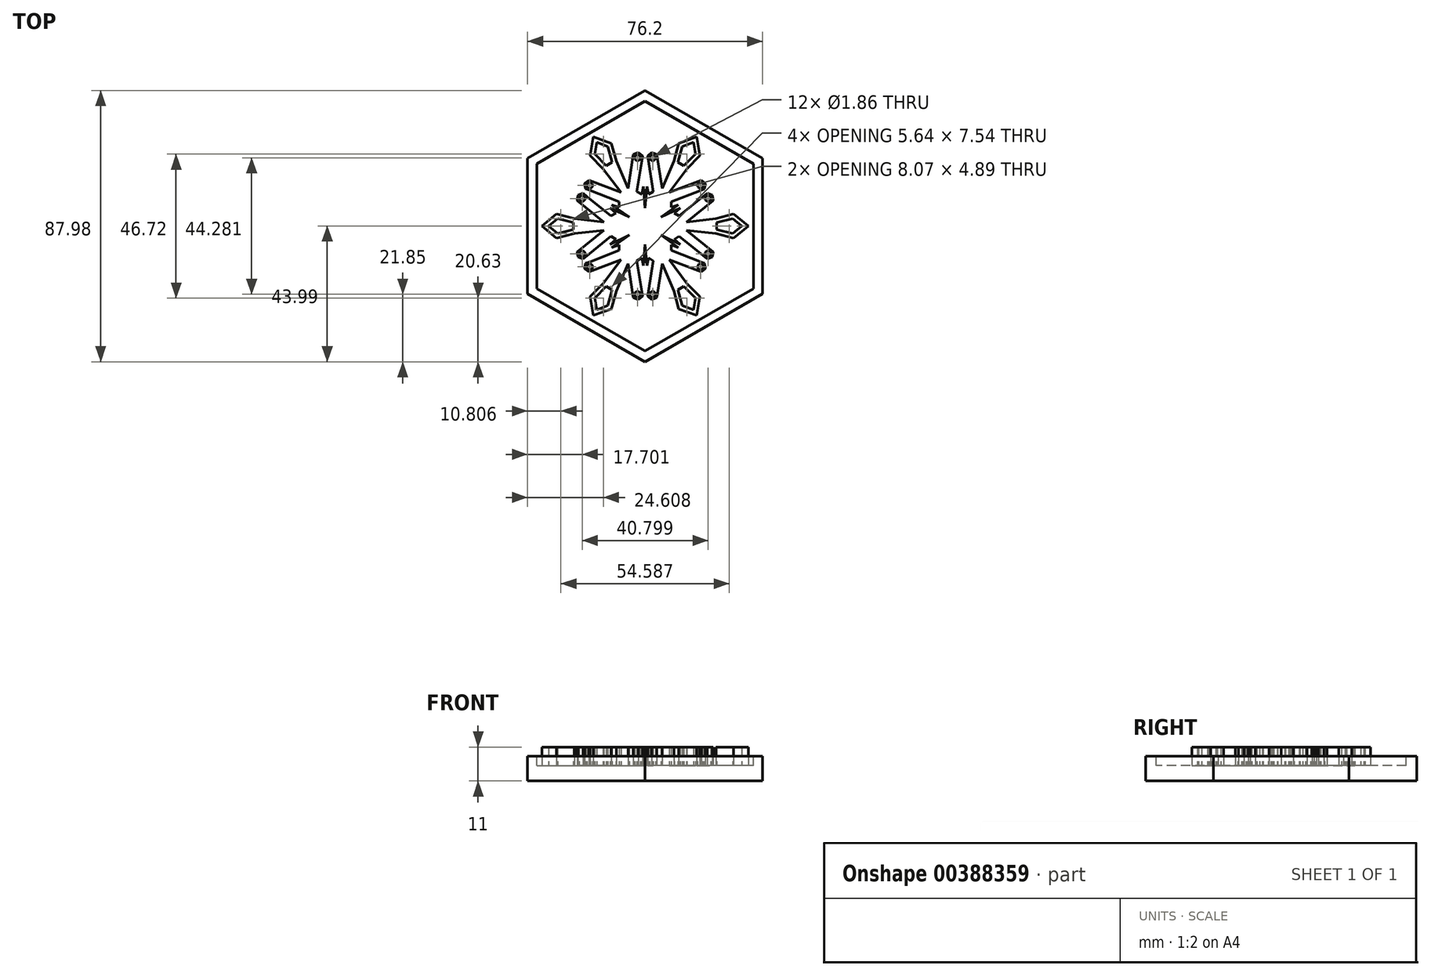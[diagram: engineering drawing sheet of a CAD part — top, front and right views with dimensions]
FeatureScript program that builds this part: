
annotation { "Feature Type Name" : "Feature", "Feature Type Description" : "" }
export const myFeature = defineFeature(function(context is Context, id is Id, definition is map)
    precondition{}
    {
        {
            var Q0;
            Q0=qCreatedBy(makeId("Top.planeOp"),FACE);
            var sketch = newSketch(context, id + "F0", { "sketchPlane" : qUnion([Q0])});
            skCircle(sketch, "E0.cCircle", {"center": v(0, 0) * mm, "radius": 38.1 * mm, "construction": true});
            skLineSegment(sketch, "E0.0", {"start": v(0, 44) * mm, "end": v(38.1, 22) * mm});
            skLineSegment(sketch, "E0.1", {"start": v(38.1, 22) * mm, "end": v(38.1, -22) * mm});
            skLineSegment(sketch, "E0.2", {"start": v(38.1, -22) * mm, "end": v(0, -44) * mm});
            skLineSegment(sketch, "E0.3", {"start": v(0, -44) * mm, "end": v(-38.1, -22) * mm});
            skLineSegment(sketch, "E0.4", {"start": v(-38.1, -22) * mm, "end": v(-38.1, 22) * mm});
            skLineSegment(sketch, "E0.5", {"start": v(-38.1, 22) * mm, "end": v(0, 44) * mm});
            skPoint(sketch, "E0.0.midPoint", {"position": v(19.05, 33) * mm});
            skLineSegment(sketch, "E1", {"start": v(0, 44) * mm, "end": v(0, -44) * mm, "construction": true});
            skLineSegment(sketch, "E2.0", {"start": v(35.1, 20.26) * mm, "end": v(35.1, -20.26) * mm});
            skLineSegment(sketch, "E2.1", {"start": v(0, -40.53) * mm, "end": v(-35.1, -20.26) * mm});
            skLineSegment(sketch, "E2.2", {"start": v(-35.1, -20.26) * mm, "end": v(-35.1, 20.26) * mm});
            skLineSegment(sketch, "E2.3", {"start": v(35.1, -20.26) * mm, "end": v(0, -40.53) * mm});
            skLineSegment(sketch, "E2.4", {"start": v(-35.1, 20.26) * mm, "end": v(0, 40.53) * mm});
            skLineSegment(sketch, "E2.5", {"start": v(0, 40.53) * mm, "end": v(35.1, 20.26) * mm});
            skSolve(sketch);
        }
        {
            var Q0;
            Q0 = qSketchRegion(id + "F0", true);
            var Q1;
            Q1=makeQuery(id+"F0.imprint","IMPRINT",FACE,{"disambiguationData":[TD([[makeQuery(id+"F0.imprint","IMPRINT",EDGE,{"derivedFrom":sQuery(id+"F0.wireOp",EDGE,"E2.0")}),-1.0]])]});
            extrude(context, id + "F1", {"entities" : qUnion([Q0, Q1]), "oppositeDirection" : true, "depth" : 8 * mm});
        }
        {
            var Q0;
            Q0=makeQuery(id+"F0.imprint","IMPRINT",FACE,{"disambiguationData":[TD([[makeQuery(id+"F0.imprint","IMPRINT",EDGE,{"derivedFrom":sQuery(id+"F0.wireOp",EDGE,"E2.0")}),-1.0]])]});
            extrude(context, id + "F2", {"entities" : qUnion([Q0]), "operationType" : NewBodyOperationType.REMOVE, "oppositeDirection" : true, "depth" : 3 * mm});
        }
        {
            var Q0;
            Q0=makeQuery(id+"F2.boolean.opBoolean","COPY",FACE,{"derivedFrom":makeQuery(id+"F2.opExtrude","CAP_FACE",FACE,{"disambiguationData":[OSD([sQuery(id+"F0.wireOp",EDGE,"E2.0"),sQuery(id+"F0.wireOp",EDGE,"E2.1"),sQuery(id+"F0.wireOp",EDGE,"E2.2"),sQuery(id+"F0.wireOp",EDGE,"E2.3"),sQuery(id+"F0.wireOp",EDGE,"E2.4"),sQuery(id+"F0.wireOp",EDGE,"E2.5")])],"isStart":false})});
            var sketch = newSketch(context, id + "F3", { "sketchPlane" : qUnion([Q0])});
            skLineSegment(sketch, "E3.0", {"start": v(0, 5.78) * mm, "end": v(5, 2.9) * mm});
            skLineSegment(sketch, "E3.1", {"start": v(5, 2.9) * mm, "end": v(5, -2.88) * mm});
            skLineSegment(sketch, "E3.2", {"start": v(5, -2.88) * mm, "end": v(0, -5.76) * mm});
            skLineSegment(sketch, "E3.3", {"start": v(0, -5.76) * mm, "end": v(-5, -2.88) * mm});
            skLineSegment(sketch, "E3.4", {"start": v(-5, -2.88) * mm, "end": v(-5, 2.9) * mm});
            skLineSegment(sketch, "E3.5", {"start": v(-5, 2.9) * mm, "end": v(0, 5.78) * mm});
            skPoint(sketch, "E3.0.midPoint", {"position": v(2.5, 4.34) * mm});
            skLineSegment(sketch, "E4", {"start": v(-16.74, -29) * mm, "end": v(0, 0) * mm, "construction": true});
            skLineSegment(sketch, "E5", {"start": v(-16.74, -29) * mm, "end": v(-17.8, -22.9) * mm});
            skLineSegment(sketch, "E6", {"start": v(-17.8, -22.9) * mm, "end": v(-13.57, -18.62) * mm});
            skLineSegment(sketch, "E7", {"start": v(-13.57, -18.62) * mm, "end": v(-7.83, -10.9) * mm});
            skLineSegment(sketch, "E8", {"start": v(-8.4, -7.92) * mm, "end": v(-8.4, -6.07) * mm});
            skLineSegment(sketch, "E9", {"start": v(-8.4, -6.07) * mm, "end": v(-10.81, -6.92) * mm});
            skLineSegment(sketch, "E10", {"start": v(-10.81, -6.92) * mm, "end": v(-5, -2.88) * mm});
            skLineSegment(sketch, "E11.MirrorCS", {"start": v(-16.74, -29) * mm, "end": v(-10.93, -26.86) * mm});
            skLineSegment(sketch, "E12.MirrorCS", {"start": v(-10.93, -26.86) * mm, "end": v(-9.34, -21.06) * mm});
            skLineSegment(sketch, "E13.MirrorCS", {"start": v(-9.34, -21.06) * mm, "end": v(-5.52, -12.23) * mm});
            skLineSegment(sketch, "E14.MirrorCS", {"start": v(-2.65, -11.24) * mm, "end": v(-1.06, -10.32) * mm});
            skLineSegment(sketch, "E15.MirrorCS", {"start": v(-1.06, -10.32) * mm, "end": v(-0.59, -12.83) * mm});
            skLineSegment(sketch, "E16.MirrorCS", {"start": v(-0.59, -12.83) * mm, "end": v(0.01, -5.77) * mm});
            skPoint(sketch, "E17.center", {"position": v(0, 0) * mm});
            skLineSegment(sketch, "E18", {"start": v(-7.83, -10.9) * mm, "end": v(-17.41, -14.6) * mm});
            skLineSegment(sketch, "E19", {"start": v(-18.49, -11.8) * mm, "end": v(-8.4, -7.92) * mm});
            skArc(sketch, "E20.cCircle", {"start": v(-18.49, -11.8) * mm, "mid": v(-18.49, -11.8) * mm, "end": v(-18.49, -11.8) * mm, "construction": true});
            skLineSegment(sketch, "E20.0", {"start": v(-19.3, -12.1) * mm, "end": v(-17.68, -11.48) * mm});
            skLineSegment(sketch, "E20.1", {"start": v(-17.68, -11.48) * mm, "end": v(-17.68, -11.48) * mm});
            skLineSegment(sketch, "E20.3", {"start": v(-16.6, -14.28) * mm, "end": v(-18.22, -14.9) * mm});
            skLineSegment(sketch, "E20.4", {"start": v(-18.22, -14.9) * mm, "end": v(-19.57, -13.81) * mm});
            skLineSegment(sketch, "E20.5", {"start": v(-19.57, -13.81) * mm, "end": v(-19.3, -12.1) * mm});
            skPoint(sketch, "E20.0.midPoint", {"position": v(-18.49, -11.8) * mm});
            skPoint(sketch, "E21.orphan", {"position": v(-16.33, -12.57) * mm});
            skLineSegment(sketch, "E22.MirrorCS", {"start": v(-5.52, -12.23) * mm, "end": v(-3.93, -22.37) * mm});
            skLineSegment(sketch, "E23.MirrorCS", {"start": v(-3.8, -23.23) * mm, "end": v(-2.18, -23.85) * mm});
            skLineSegment(sketch, "E24.MirrorCS", {"start": v(-2.18, -23.85) * mm, "end": v(-0.83, -22.76) * mm});
            skLineSegment(sketch, "E25.MirrorCS", {"start": v(-0.97, -21.9) * mm, "end": v(-2.65, -11.24) * mm});
            skLineSegment(sketch, "E26.MirrorCS", {"start": v(-4.06, -21.52) * mm, "end": v(-3.8, -23.23) * mm});
            skLineSegment(sketch, "E27.MirrorCS", {"start": v(-0.83, -22.76) * mm, "end": v(-1.1, -21.05) * mm});
            skLineSegment(sketch, "E28.0", {"start": v(-16.31, -23.36) * mm, "end": v(-12.59, -19.59) * mm});
            skLineSegment(sketch, "E28.1", {"start": v(-15.66, -27.13) * mm, "end": v(-16.31, -23.36) * mm});
            skLineSegment(sketch, "E28.2", {"start": v(-15.66, -27.13) * mm, "end": v(-12.08, -25.8) * mm});
            skLineSegment(sketch, "E28.3", {"start": v(-12.08, -25.8) * mm, "end": v(-10.67, -20.7) * mm});
            skLineSegment(sketch, "E29", {"start": v(-12.59, -19.59) * mm, "end": v(-10.67, -20.7) * mm});
            skLineSegment(sketch, "E30", {"start": v(-2.18, -23.85) * mm, "end": v(-2.8, -19.92) * mm, "construction": true});
            skLineSegment(sketch, "E31", {"start": v(-2.8, -19.92) * mm, "end": v(-0.97, -21.9) * mm, "construction": true});
            skLineSegment(sketch, "E32", {"start": v(-0.97, -21.9) * mm, "end": v(-3.93, -22.37) * mm, "construction": true});
            skCircle(sketch, "E33", {"center": v(-2.45, -22.14) * mm, "radius": 0.93 * mm});
            skCircle(sketch, "E34.MirrorC", {"center": v(-17.95, -13.2) * mm, "radius": 0.93 * mm});
            skLineSegment(sketch, "E35.0", {"start": v(-7.4, -7.92) * mm, "end": v(-7.4, -5.77) * mm});
            skLineSegment(sketch, "E36.0", {"start": v(-3.15, -10.37) * mm, "end": v(-1.3, -9.3) * mm});
            skLineSegment(sketch, "E37.0", {"start": v(-1.3, -9.3) * mm, "end": v(-1.04, -6.32) * mm});
            skLineSegment(sketch, "E38.0", {"start": v(-1.04, -6.32) * mm, "end": v(-4.95, -4.06) * mm});
            skLineSegment(sketch, "E39.trimOffspring", {"start": v(-7.4, -5.77) * mm, "end": v(-4.95, -4.06) * mm});
            skLineSegment(sketch, "E40", {"start": v(-7.4, -7.92) * mm, "end": v(-6.38, -11.05) * mm});
            skLineSegment(sketch, "E41.MirrorCS", {"start": v(-3.15, -10.37) * mm, "end": v(-6.38, -11.05) * mm});
            skLineSegment(sketch, "E42.1.1", {"start": v(16.74, -29) * mm, "end": v(17.8, -22.9) * mm});
            skLineSegment(sketch, "E42.1.2", {"start": v(0.97, -21.9) * mm, "end": v(2.65, -11.24) * mm});
            skLineSegment(sketch, "E42.1.3", {"start": v(13.57, -18.62) * mm, "end": v(7.83, -10.9) * mm});
            skPoint(sketch, "E42.1.4", {"position": v(2.72, -20.43) * mm});
            skPoint(sketch, "E42.1.5", {"position": v(0.97, -21.9) * mm});
            skLineSegment(sketch, "E42.1.6", {"start": v(7.4, -7.92) * mm, "end": v(6.38, -11.05) * mm});
            skLineSegment(sketch, "E42.1.7", {"start": v(17.8, -22.9) * mm, "end": v(13.57, -18.62) * mm});
            skLineSegment(sketch, "E42.1.8", {"start": v(1.3, -9.3) * mm, "end": v(1.04, -6.32) * mm});
            skLineSegment(sketch, "E42.1.9", {"start": v(7.83, -10.9) * mm, "end": v(17.41, -14.6) * mm});
            skLineSegment(sketch, "E42.1.10", {"start": v(18.49, -11.8) * mm, "end": v(8.4, -7.92) * mm});
            skLineSegment(sketch, "E42.1.11", {"start": v(12.08, -25.8) * mm, "end": v(10.67, -20.7) * mm});
            skLineSegment(sketch, "E42.1.12", {"start": v(3.15, -10.37) * mm, "end": v(6.38, -11.05) * mm});
            skLineSegment(sketch, "E42.1.13", {"start": v(0.59, -12.83) * mm, "end": v(-0.01, -5.77) * mm});
            skLineSegment(sketch, "E42.1.14", {"start": v(9.34, -21.06) * mm, "end": v(5.52, -12.23) * mm});
            skLineSegment(sketch, "E42.1.15", {"start": v(15.66, -27.13) * mm, "end": v(16.31, -23.36) * mm});
            skLineSegment(sketch, "E42.1.16", {"start": v(10.93, -26.86) * mm, "end": v(9.34, -21.06) * mm});
            skLineSegment(sketch, "E42.1.17", {"start": v(16.74, -29) * mm, "end": v(10.93, -26.86) * mm});
            skLineSegment(sketch, "E42.1.18", {"start": v(5.52, -12.23) * mm, "end": v(3.93, -22.37) * mm});
            skLineSegment(sketch, "E42.1.19", {"start": v(16.31, -23.36) * mm, "end": v(12.59, -19.59) * mm});
            skLineSegment(sketch, "E42.1.20", {"start": v(15.66, -27.13) * mm, "end": v(12.08, -25.8) * mm});
            skLineSegment(sketch, "E42.1.21", {"start": v(4.06, -21.52) * mm, "end": v(3.8, -23.23) * mm});
            skCircle(sketch, "E42.1.22", {"center": v(2.45, -22.14) * mm, "radius": 0.93 * mm});
            skLineSegment(sketch, "E42.1.23", {"start": v(19.57, -13.81) * mm, "end": v(15.85, -12.39) * mm, "construction": true});
            skLineSegment(sketch, "E42.1.24", {"start": v(16.6, -14.28) * mm, "end": v(18.22, -14.9) * mm});
            skLineSegment(sketch, "E42.1.25", {"start": v(3.8, -23.23) * mm, "end": v(2.18, -23.85) * mm});
            skCircle(sketch, "E42.1.26", {"center": v(17.95, -13.2) * mm, "radius": 0.93 * mm});
            skLineSegment(sketch, "E42.1.27", {"start": v(15.85, -12.39) * mm, "end": v(18.49, -11.8) * mm, "construction": true});
            skLineSegment(sketch, "E42.1.28", {"start": v(2.18, -23.85) * mm, "end": v(0.83, -22.76) * mm});
            skLineSegment(sketch, "E42.1.29", {"start": v(2.65, -11.24) * mm, "end": v(1.06, -10.32) * mm});
            skLineSegment(sketch, "E42.1.30", {"start": v(19.57, -13.81) * mm, "end": v(19.3, -12.1) * mm});
            skLineSegment(sketch, "E42.1.31", {"start": v(7.4, -7.92) * mm, "end": v(7.4, -5.77) * mm});
            skLineSegment(sketch, "E42.1.32", {"start": v(10.67, -20.7) * mm, "end": v(12.59, -19.59) * mm});
            skLineSegment(sketch, "E42.1.33", {"start": v(8.4, -6.07) * mm, "end": v(10.81, -6.92) * mm});
            skLineSegment(sketch, "E42.1.34", {"start": v(18.49, -11.8) * mm, "end": v(17.41, -14.6) * mm, "construction": true});
            skLineSegment(sketch, "E42.1.35", {"start": v(3.15, -10.37) * mm, "end": v(1.3, -9.3) * mm});
            skLineSegment(sketch, "E42.1.36", {"start": v(8.4, -7.92) * mm, "end": v(8.4, -6.07) * mm});
            skLineSegment(sketch, "E42.1.37", {"start": v(1.06, -10.32) * mm, "end": v(0.59, -12.83) * mm});
            skLineSegment(sketch, "E42.1.38", {"start": v(19.3, -12.1) * mm, "end": v(17.68, -11.48) * mm});
            skLineSegment(sketch, "E42.1.39", {"start": v(18.22, -14.9) * mm, "end": v(19.57, -13.81) * mm});
            skLineSegment(sketch, "E42.1.40", {"start": v(0.83, -22.76) * mm, "end": v(1.1, -21.05) * mm});
            skLineSegment(sketch, "E42.1.41", {"start": v(1.1, -21.05) * mm, "end": v(1.1, -21.05) * mm});
            skArc(sketch, "E42.1.42", {"start": v(0.97, -21.9) * mm, "mid": v(0.97, -21.9) * mm, "end": v(0.97, -21.9) * mm, "construction": true});
            skLineSegment(sketch, "E42.1.43", {"start": v(10.81, -6.92) * mm, "end": v(5, -2.88) * mm});
            skLineSegment(sketch, "E42.1.44", {"start": v(7.4, -5.77) * mm, "end": v(4.95, -4.06) * mm});
            skLineSegment(sketch, "E42.1.45", {"start": v(4.95, -4.06) * mm, "end": v(1.04, -6.32) * mm});
            skLineSegment(sketch, "E42.2.1", {"start": v(33.49, 0) * mm, "end": v(28.73, 3.96) * mm});
            skLineSegment(sketch, "E42.2.2", {"start": v(19.46, -10.12) * mm, "end": v(11.06, -3.32) * mm});
            skLineSegment(sketch, "E42.2.3", {"start": v(22.9, 2.44) * mm, "end": v(13.36, 1.33) * mm});
            skPoint(sketch, "E42.2.4", {"position": v(19.05, -7.86) * mm});
            skPoint(sketch, "E42.2.5", {"position": v(19.46, -10.12) * mm});
            skLineSegment(sketch, "E42.2.6", {"start": v(10.56, 2.45) * mm, "end": v(12.76, 0) * mm});
            skLineSegment(sketch, "E42.2.7", {"start": v(28.73, 3.96) * mm, "end": v(22.9, 2.44) * mm});
            skLineSegment(sketch, "E42.2.8", {"start": v(8.7, -3.53) * mm, "end": v(6, -2.26) * mm});
            skLineSegment(sketch, "E42.2.9", {"start": v(13.36, 1.33) * mm, "end": v(21.34, 7.78) * mm});
            skLineSegment(sketch, "E42.2.10", {"start": v(19.46, 10.12) * mm, "end": v(11.06, 3.32) * mm});
            skLineSegment(sketch, "E42.2.11", {"start": v(28.4, -2.45) * mm, "end": v(23.26, -1.1) * mm});
            skLineSegment(sketch, "E42.2.12", {"start": v(10.56, -2.45) * mm, "end": v(12.76, 0) * mm});
            skLineSegment(sketch, "E42.2.13", {"start": v(11.4, -5.9) * mm, "end": v(5, -2.9) * mm});
            skLineSegment(sketch, "E42.2.14", {"start": v(22.9, -2.44) * mm, "end": v(13.36, -1.33) * mm});
            skLineSegment(sketch, "E42.2.15", {"start": v(31.33, 0) * mm, "end": v(28.4, 2.45) * mm});
            skLineSegment(sketch, "E42.2.16", {"start": v(28.73, -3.96) * mm, "end": v(22.9, -2.44) * mm});
            skLineSegment(sketch, "E42.2.17", {"start": v(33.49, 0) * mm, "end": v(28.73, -3.96) * mm});
            skLineSegment(sketch, "E42.2.18", {"start": v(13.36, -1.33) * mm, "end": v(21.34, -7.78) * mm});
            skLineSegment(sketch, "E42.2.19", {"start": v(28.4, 2.45) * mm, "end": v(23.26, 1.1) * mm});
            skLineSegment(sketch, "E42.2.20", {"start": v(31.33, 0) * mm, "end": v(28.4, -2.45) * mm});
            skLineSegment(sketch, "E42.2.21", {"start": v(20.67, -7.24) * mm, "end": v(22.01, -8.33) * mm});
            skCircle(sketch, "E42.2.22", {"center": v(20.4, -8.95) * mm, "radius": 0.93 * mm});
            skLineSegment(sketch, "E42.2.23", {"start": v(21.75, 10.04) * mm, "end": v(18.65, 7.53) * mm, "construction": true});
            skLineSegment(sketch, "E42.2.24", {"start": v(20.67, 7.24) * mm, "end": v(22.01, 8.33) * mm});
            skLineSegment(sketch, "E42.2.25", {"start": v(22.01, -8.33) * mm, "end": v(21.75, -10.04) * mm});
            skCircle(sketch, "E42.2.26", {"center": v(20.4, 8.95) * mm, "radius": 0.93 * mm});
            skLineSegment(sketch, "E42.2.27", {"start": v(18.65, 7.53) * mm, "end": v(19.46, 10.12) * mm, "construction": true});
            skLineSegment(sketch, "E42.2.28", {"start": v(21.75, -10.04) * mm, "end": v(20.13, -10.66) * mm});
            skLineSegment(sketch, "E42.2.29", {"start": v(11.06, -3.32) * mm, "end": v(9.46, -4.24) * mm});
            skLineSegment(sketch, "E42.2.30", {"start": v(21.75, 10.04) * mm, "end": v(20.13, 10.66) * mm});
            skLineSegment(sketch, "E42.2.31", {"start": v(10.56, 2.45) * mm, "end": v(8.7, 3.53) * mm});
            skLineSegment(sketch, "E42.2.32", {"start": v(23.26, -1.1) * mm, "end": v(23.26, 1.1) * mm});
            skLineSegment(sketch, "E42.2.33", {"start": v(9.46, 4.24) * mm, "end": v(11.4, 5.9) * mm});
            skLineSegment(sketch, "E42.2.34", {"start": v(19.46, 10.12) * mm, "end": v(21.34, 7.78) * mm, "construction": true});
            skLineSegment(sketch, "E42.2.35", {"start": v(10.56, -2.45) * mm, "end": v(8.7, -3.53) * mm});
            skLineSegment(sketch, "E42.2.36", {"start": v(11.06, 3.32) * mm, "end": v(9.46, 4.24) * mm});
            skLineSegment(sketch, "E42.2.37", {"start": v(9.46, -4.24) * mm, "end": v(11.4, -5.9) * mm});
            skLineSegment(sketch, "E42.2.38", {"start": v(20.13, 10.66) * mm, "end": v(18.78, 9.57) * mm});
            skLineSegment(sketch, "E42.2.39", {"start": v(22.01, 8.33) * mm, "end": v(21.75, 10.04) * mm});
            skLineSegment(sketch, "E42.2.40", {"start": v(20.13, -10.66) * mm, "end": v(18.78, -9.57) * mm});
            skLineSegment(sketch, "E42.2.41", {"start": v(18.78, -9.57) * mm, "end": v(18.78, -9.57) * mm});
            skArc(sketch, "E42.2.42", {"start": v(19.45, -10.11) * mm, "mid": v(19.45, -10.11) * mm, "end": v(19.46, -10.12) * mm, "construction": true});
            skLineSegment(sketch, "E42.2.43", {"start": v(11.4, 5.9) * mm, "end": v(5, 2.9) * mm});
            skLineSegment(sketch, "E42.2.44", {"start": v(8.7, 3.53) * mm, "end": v(6, 2.26) * mm});
            skLineSegment(sketch, "E42.2.45", {"start": v(6, 2.26) * mm, "end": v(6, -2.26) * mm});
            skLineSegment(sketch, "E42.3.1", {"start": v(16.74, 29) * mm, "end": v(10.93, 26.86) * mm});
            skLineSegment(sketch, "E42.3.2", {"start": v(18.49, 11.8) * mm, "end": v(8.4, 7.92) * mm});
            skLineSegment(sketch, "E42.3.3", {"start": v(9.34, 21.06) * mm, "end": v(5.52, 12.23) * mm});
            skPoint(sketch, "E42.3.4", {"position": v(16.33, 12.57) * mm});
            skPoint(sketch, "E42.3.5", {"position": v(18.49, 11.8) * mm});
            skLineSegment(sketch, "E42.3.6", {"start": v(3.15, 10.37) * mm, "end": v(6.38, 11.05) * mm});
            skLineSegment(sketch, "E42.3.7", {"start": v(10.93, 26.86) * mm, "end": v(9.34, 21.06) * mm});
            skLineSegment(sketch, "E42.3.8", {"start": v(7.4, 5.77) * mm, "end": v(4.95, 4.06) * mm});
            skLineSegment(sketch, "E42.3.9", {"start": v(5.52, 12.23) * mm, "end": v(3.93, 22.37) * mm});
            skLineSegment(sketch, "E42.3.10", {"start": v(0.97, 21.9) * mm, "end": v(2.65, 11.24) * mm});
            skLineSegment(sketch, "E42.3.11", {"start": v(16.31, 23.36) * mm, "end": v(12.59, 19.59) * mm});
            skLineSegment(sketch, "E42.3.12", {"start": v(7.4, 7.92) * mm, "end": v(6.38, 11.05) * mm});
            skLineSegment(sketch, "E42.3.13", {"start": v(10.81, 6.92) * mm, "end": v(5, 2.88) * mm});
            skLineSegment(sketch, "E42.3.14", {"start": v(13.57, 18.62) * mm, "end": v(7.83, 10.9) * mm});
            skLineSegment(sketch, "E42.3.15", {"start": v(15.66, 27.13) * mm, "end": v(12.08, 25.8) * mm});
            skLineSegment(sketch, "E42.3.16", {"start": v(17.8, 22.9) * mm, "end": v(13.57, 18.62) * mm});
            skLineSegment(sketch, "E42.3.17", {"start": v(16.74, 29) * mm, "end": v(17.8, 22.9) * mm});
            skLineSegment(sketch, "E42.3.18", {"start": v(7.83, 10.9) * mm, "end": v(17.41, 14.6) * mm});
            skLineSegment(sketch, "E42.3.19", {"start": v(12.08, 25.8) * mm, "end": v(10.67, 20.7) * mm});
            skLineSegment(sketch, "E42.3.20", {"start": v(15.66, 27.13) * mm, "end": v(16.31, 23.36) * mm});
            skLineSegment(sketch, "E42.3.21", {"start": v(16.6, 14.28) * mm, "end": v(18.22, 14.9) * mm});
            skCircle(sketch, "E42.3.22", {"center": v(17.95, 13.2) * mm, "radius": 0.93 * mm});
            skLineSegment(sketch, "E42.3.23", {"start": v(2.18, 23.85) * mm, "end": v(2.8, 19.92) * mm, "construction": true});
            skLineSegment(sketch, "E42.3.24", {"start": v(4.06, 21.52) * mm, "end": v(3.8, 23.23) * mm});
            skLineSegment(sketch, "E42.3.25", {"start": v(18.22, 14.9) * mm, "end": v(19.57, 13.81) * mm});
            skCircle(sketch, "E42.3.26", {"center": v(2.45, 22.14) * mm, "radius": 0.93 * mm});
            skLineSegment(sketch, "E42.3.27", {"start": v(2.8, 19.92) * mm, "end": v(0.97, 21.9) * mm, "construction": true});
            skLineSegment(sketch, "E42.3.28", {"start": v(19.57, 13.81) * mm, "end": v(19.3, 12.1) * mm});
            skLineSegment(sketch, "E42.3.29", {"start": v(8.4, 7.92) * mm, "end": v(8.4, 6.07) * mm});
            skLineSegment(sketch, "E42.3.30", {"start": v(2.18, 23.85) * mm, "end": v(0.83, 22.76) * mm});
            skLineSegment(sketch, "E42.3.31", {"start": v(3.15, 10.37) * mm, "end": v(1.3, 9.3) * mm});
            skLineSegment(sketch, "E42.3.32", {"start": v(12.59, 19.59) * mm, "end": v(10.67, 20.7) * mm});
            skLineSegment(sketch, "E42.3.33", {"start": v(1.06, 10.32) * mm, "end": v(0.59, 12.83) * mm});
            skLineSegment(sketch, "E42.3.34", {"start": v(0.97, 21.9) * mm, "end": v(3.93, 22.37) * mm, "construction": true});
            skLineSegment(sketch, "E42.3.35", {"start": v(7.4, 7.92) * mm, "end": v(7.4, 5.77) * mm});
            skLineSegment(sketch, "E42.3.36", {"start": v(2.65, 11.24) * mm, "end": v(1.06, 10.32) * mm});
            skLineSegment(sketch, "E42.3.37", {"start": v(8.4, 6.07) * mm, "end": v(10.81, 6.92) * mm});
            skLineSegment(sketch, "E42.3.38", {"start": v(0.83, 22.76) * mm, "end": v(1.1, 21.05) * mm});
            skLineSegment(sketch, "E42.3.39", {"start": v(3.8, 23.23) * mm, "end": v(2.18, 23.85) * mm});
            skLineSegment(sketch, "E42.3.40", {"start": v(19.3, 12.1) * mm, "end": v(17.68, 11.48) * mm});
            skLineSegment(sketch, "E42.3.41", {"start": v(17.68, 11.48) * mm, "end": v(17.68, 11.48) * mm});
            skArc(sketch, "E42.3.42", {"start": v(18.49, 11.8) * mm, "mid": v(18.49, 11.8) * mm, "end": v(18.49, 11.8) * mm, "construction": true});
            skLineSegment(sketch, "E42.3.43", {"start": v(0.59, 12.83) * mm, "end": v(-0.01, 5.77) * mm});
            skLineSegment(sketch, "E42.3.44", {"start": v(1.3, 9.3) * mm, "end": v(1.04, 6.32) * mm});
            skLineSegment(sketch, "E42.3.45", {"start": v(1.04, 6.32) * mm, "end": v(4.95, 4.06) * mm});
            skLineSegment(sketch, "E42.4.1", {"start": v(-16.74, 29) * mm, "end": v(-17.8, 22.9) * mm});
            skLineSegment(sketch, "E42.4.2", {"start": v(-0.97, 21.9) * mm, "end": v(-2.65, 11.24) * mm});
            skLineSegment(sketch, "E42.4.3", {"start": v(-13.57, 18.62) * mm, "end": v(-7.83, 10.9) * mm});
            skPoint(sketch, "E42.4.4", {"position": v(-2.72, 20.43) * mm});
            skPoint(sketch, "E42.4.5", {"position": v(-0.97, 21.9) * mm});
            skLineSegment(sketch, "E42.4.6", {"start": v(-7.4, 7.92) * mm, "end": v(-6.38, 11.05) * mm});
            skLineSegment(sketch, "E42.4.7", {"start": v(-17.8, 22.9) * mm, "end": v(-13.57, 18.62) * mm});
            skLineSegment(sketch, "E42.4.8", {"start": v(-1.3, 9.3) * mm, "end": v(-1.04, 6.32) * mm});
            skLineSegment(sketch, "E42.4.9", {"start": v(-7.83, 10.9) * mm, "end": v(-17.41, 14.6) * mm});
            skLineSegment(sketch, "E42.4.10", {"start": v(-18.49, 11.8) * mm, "end": v(-8.4, 7.92) * mm});
            skLineSegment(sketch, "E42.4.11", {"start": v(-12.08, 25.8) * mm, "end": v(-10.67, 20.7) * mm});
            skLineSegment(sketch, "E42.4.12", {"start": v(-3.15, 10.37) * mm, "end": v(-6.38, 11.05) * mm});
            skLineSegment(sketch, "E42.4.13", {"start": v(-0.59, 12.83) * mm, "end": v(0.01, 5.77) * mm});
            skLineSegment(sketch, "E42.4.14", {"start": v(-9.34, 21.06) * mm, "end": v(-5.52, 12.23) * mm});
            skLineSegment(sketch, "E42.4.15", {"start": v(-15.66, 27.13) * mm, "end": v(-16.31, 23.36) * mm});
            skLineSegment(sketch, "E42.4.16", {"start": v(-10.93, 26.86) * mm, "end": v(-9.34, 21.06) * mm});
            skLineSegment(sketch, "E42.4.17", {"start": v(-16.74, 29) * mm, "end": v(-10.93, 26.86) * mm});
            skLineSegment(sketch, "E42.4.18", {"start": v(-5.52, 12.23) * mm, "end": v(-3.93, 22.37) * mm});
            skLineSegment(sketch, "E42.4.19", {"start": v(-16.31, 23.36) * mm, "end": v(-12.59, 19.59) * mm});
            skLineSegment(sketch, "E42.4.20", {"start": v(-15.66, 27.13) * mm, "end": v(-12.08, 25.8) * mm});
            skLineSegment(sketch, "E42.4.21", {"start": v(-4.06, 21.52) * mm, "end": v(-3.8, 23.23) * mm});
            skCircle(sketch, "E42.4.22", {"center": v(-2.45, 22.14) * mm, "radius": 0.93 * mm});
            skLineSegment(sketch, "E42.4.23", {"start": v(-19.57, 13.81) * mm, "end": v(-15.85, 12.39) * mm, "construction": true});
            skLineSegment(sketch, "E42.4.24", {"start": v(-16.6, 14.28) * mm, "end": v(-18.22, 14.9) * mm});
            skLineSegment(sketch, "E42.4.25", {"start": v(-3.8, 23.23) * mm, "end": v(-2.18, 23.85) * mm});
            skCircle(sketch, "E42.4.26", {"center": v(-17.95, 13.2) * mm, "radius": 0.93 * mm});
            skLineSegment(sketch, "E42.4.27", {"start": v(-15.85, 12.39) * mm, "end": v(-18.49, 11.8) * mm, "construction": true});
            skLineSegment(sketch, "E42.4.28", {"start": v(-2.18, 23.85) * mm, "end": v(-0.83, 22.76) * mm});
            skLineSegment(sketch, "E42.4.29", {"start": v(-2.65, 11.24) * mm, "end": v(-1.06, 10.32) * mm});
            skLineSegment(sketch, "E42.4.30", {"start": v(-19.57, 13.81) * mm, "end": v(-19.3, 12.1) * mm});
            skLineSegment(sketch, "E42.4.31", {"start": v(-7.4, 7.92) * mm, "end": v(-7.4, 5.77) * mm});
            skLineSegment(sketch, "E42.4.32", {"start": v(-10.67, 20.7) * mm, "end": v(-12.59, 19.59) * mm});
            skLineSegment(sketch, "E42.4.33", {"start": v(-8.4, 6.07) * mm, "end": v(-10.81, 6.92) * mm});
            skLineSegment(sketch, "E42.4.34", {"start": v(-18.49, 11.8) * mm, "end": v(-17.41, 14.6) * mm, "construction": true});
            skLineSegment(sketch, "E42.4.35", {"start": v(-3.15, 10.37) * mm, "end": v(-1.3, 9.3) * mm});
            skLineSegment(sketch, "E42.4.36", {"start": v(-8.4, 7.92) * mm, "end": v(-8.4, 6.07) * mm});
            skLineSegment(sketch, "E42.4.37", {"start": v(-1.06, 10.32) * mm, "end": v(-0.59, 12.83) * mm});
            skLineSegment(sketch, "E42.4.38", {"start": v(-19.3, 12.1) * mm, "end": v(-17.68, 11.48) * mm});
            skLineSegment(sketch, "E42.4.39", {"start": v(-18.22, 14.9) * mm, "end": v(-19.57, 13.81) * mm});
            skLineSegment(sketch, "E42.4.40", {"start": v(-0.83, 22.76) * mm, "end": v(-1.1, 21.05) * mm});
            skLineSegment(sketch, "E42.4.41", {"start": v(-1.1, 21.05) * mm, "end": v(-1.1, 21.05) * mm});
            skArc(sketch, "E42.4.42", {"start": v(-0.97, 21.9) * mm, "mid": v(-0.97, 21.9) * mm, "end": v(-0.97, 21.9) * mm, "construction": true});
            skLineSegment(sketch, "E42.4.43", {"start": v(-10.81, 6.92) * mm, "end": v(-5, 2.88) * mm});
            skLineSegment(sketch, "E42.4.44", {"start": v(-7.4, 5.77) * mm, "end": v(-4.95, 4.06) * mm});
            skLineSegment(sketch, "E42.4.45", {"start": v(-4.95, 4.06) * mm, "end": v(-1.04, 6.32) * mm});
            skLineSegment(sketch, "E42.5.1", {"start": v(-33.49, 0) * mm, "end": v(-28.73, -3.96) * mm});
            skLineSegment(sketch, "E42.5.2", {"start": v(-19.46, 10.12) * mm, "end": v(-11.06, 3.32) * mm});
            skLineSegment(sketch, "E42.5.3", {"start": v(-22.9, -2.44) * mm, "end": v(-13.36, -1.33) * mm});
            skPoint(sketch, "E42.5.4", {"position": v(-19.05, 7.86) * mm});
            skPoint(sketch, "E42.5.5", {"position": v(-19.46, 10.12) * mm});
            skLineSegment(sketch, "E42.5.6", {"start": v(-10.56, -2.45) * mm, "end": v(-12.76, 0) * mm});
            skLineSegment(sketch, "E42.5.7", {"start": v(-28.73, -3.96) * mm, "end": v(-22.9, -2.44) * mm});
            skLineSegment(sketch, "E42.5.8", {"start": v(-8.7, 3.53) * mm, "end": v(-6, 2.26) * mm});
            skLineSegment(sketch, "E42.5.9", {"start": v(-13.36, -1.33) * mm, "end": v(-21.34, -7.78) * mm});
            skLineSegment(sketch, "E42.5.10", {"start": v(-19.46, -10.12) * mm, "end": v(-11.06, -3.32) * mm});
            skLineSegment(sketch, "E42.5.11", {"start": v(-28.4, 2.45) * mm, "end": v(-23.26, 1.1) * mm});
            skLineSegment(sketch, "E42.5.12", {"start": v(-10.56, 2.45) * mm, "end": v(-12.76, 0) * mm});
            skLineSegment(sketch, "E42.5.13", {"start": v(-11.4, 5.9) * mm, "end": v(-5, 2.9) * mm});
            skLineSegment(sketch, "E42.5.14", {"start": v(-22.9, 2.44) * mm, "end": v(-13.36, 1.33) * mm});
            skLineSegment(sketch, "E42.5.15", {"start": v(-31.33, 0) * mm, "end": v(-28.4, -2.45) * mm});
            skLineSegment(sketch, "E42.5.16", {"start": v(-28.73, 3.96) * mm, "end": v(-22.9, 2.44) * mm});
            skLineSegment(sketch, "E42.5.17", {"start": v(-33.49, 0) * mm, "end": v(-28.73, 3.96) * mm});
            skLineSegment(sketch, "E42.5.18", {"start": v(-13.36, 1.33) * mm, "end": v(-21.34, 7.78) * mm});
            skLineSegment(sketch, "E42.5.19", {"start": v(-28.4, -2.45) * mm, "end": v(-23.26, -1.1) * mm});
            skLineSegment(sketch, "E42.5.20", {"start": v(-31.33, 0) * mm, "end": v(-28.4, 2.45) * mm});
            skLineSegment(sketch, "E42.5.21", {"start": v(-20.67, 7.24) * mm, "end": v(-22.01, 8.33) * mm});
            skCircle(sketch, "E42.5.22", {"center": v(-20.4, 8.95) * mm, "radius": 0.93 * mm});
            skLineSegment(sketch, "E42.5.23", {"start": v(-21.75, -10.04) * mm, "end": v(-18.65, -7.53) * mm, "construction": true});
            skLineSegment(sketch, "E42.5.24", {"start": v(-20.67, -7.24) * mm, "end": v(-22.01, -8.33) * mm});
            skLineSegment(sketch, "E42.5.25", {"start": v(-22.01, 8.33) * mm, "end": v(-21.75, 10.04) * mm});
            skCircle(sketch, "E42.5.26", {"center": v(-20.4, -8.95) * mm, "radius": 0.93 * mm});
            skLineSegment(sketch, "E42.5.27", {"start": v(-18.65, -7.53) * mm, "end": v(-19.46, -10.12) * mm, "construction": true});
            skLineSegment(sketch, "E42.5.28", {"start": v(-21.75, 10.04) * mm, "end": v(-20.13, 10.66) * mm});
            skLineSegment(sketch, "E42.5.29", {"start": v(-11.06, 3.32) * mm, "end": v(-9.46, 4.24) * mm});
            skLineSegment(sketch, "E42.5.30", {"start": v(-21.75, -10.04) * mm, "end": v(-20.13, -10.66) * mm});
            skLineSegment(sketch, "E42.5.31", {"start": v(-10.56, -2.45) * mm, "end": v(-8.7, -3.53) * mm});
            skLineSegment(sketch, "E42.5.32", {"start": v(-23.26, 1.1) * mm, "end": v(-23.26, -1.1) * mm});
            skLineSegment(sketch, "E42.5.33", {"start": v(-9.46, -4.24) * mm, "end": v(-11.4, -5.9) * mm});
            skLineSegment(sketch, "E42.5.34", {"start": v(-19.46, -10.12) * mm, "end": v(-21.34, -7.78) * mm, "construction": true});
            skLineSegment(sketch, "E42.5.35", {"start": v(-10.56, 2.45) * mm, "end": v(-8.7, 3.53) * mm});
            skLineSegment(sketch, "E42.5.36", {"start": v(-11.06, -3.32) * mm, "end": v(-9.46, -4.24) * mm});
            skLineSegment(sketch, "E42.5.37", {"start": v(-9.46, 4.24) * mm, "end": v(-11.4, 5.9) * mm});
            skLineSegment(sketch, "E42.5.38", {"start": v(-20.13, -10.66) * mm, "end": v(-18.78, -9.57) * mm});
            skLineSegment(sketch, "E42.5.39", {"start": v(-22.01, -8.33) * mm, "end": v(-21.75, -10.04) * mm});
            skLineSegment(sketch, "E42.5.40", {"start": v(-20.13, 10.66) * mm, "end": v(-18.78, 9.57) * mm});
            skLineSegment(sketch, "E42.5.41", {"start": v(-18.78, 9.57) * mm, "end": v(-18.78, 9.57) * mm});
            skArc(sketch, "E42.5.42", {"start": v(-19.45, 10.11) * mm, "mid": v(-19.45, 10.11) * mm, "end": v(-19.46, 10.12) * mm, "construction": true});
            skLineSegment(sketch, "E42.5.43", {"start": v(-11.4, -5.9) * mm, "end": v(-5, -2.9) * mm});
            skLineSegment(sketch, "E42.5.44", {"start": v(-8.7, -3.53) * mm, "end": v(-6, -2.26) * mm});
            skLineSegment(sketch, "E42.5.45", {"start": v(-6, -2.26) * mm, "end": v(-6, 2.26) * mm});
            skSolve(sketch);
        }
        {
            var Q0;
            Q0 = qSketchRegion(id + "F3", true);
            var Q1;
            Q1=makeQuery(id+"F3.imprint","IMPRINT",FACE,{"disambiguationData":[TD([[makeQuery(id+"F3.imprint","IMPRINT",EDGE,{"derivedFrom":sQuery(id+"F3.wireOp",EDGE,"E42.5.6")}),-1.0]])]});
            var Q2;
            Q2=makeQuery(id+"F3.imprint","IMPRINT",FACE,{"disambiguationData":[TD([[makeQuery(id+"F3.imprint","IMPRINT",EDGE,{"derivedFrom":sQuery(id+"F3.wireOp",EDGE,"E42.4.6")}),-1.0]])]});
            var Q3;
            Q3=makeQuery(id+"F3.imprint","IMPRINT",FACE,{"disambiguationData":[TD([[makeQuery(id+"F3.imprint","IMPRINT",EDGE,{"derivedFrom":sQuery(id+"F3.wireOp",EDGE,"E42.3.6")}),-1.0]])]});
            var Q4;
            Q4=makeQuery(id+"F3.imprint","IMPRINT",FACE,{"disambiguationData":[TD([[makeQuery(id+"F3.imprint","IMPRINT",EDGE,{"derivedFrom":sQuery(id+"F3.wireOp",EDGE,"E42.2.6")}),-1.0]])]});
            var Q5;
            Q5=makeQuery(id+"F3.imprint","IMPRINT",FACE,{"disambiguationData":[TD([[makeQuery(id+"F3.imprint","IMPRINT",EDGE,{"derivedFrom":sQuery(id+"F3.wireOp",EDGE,"E42.1.6")}),-1.0]])]});
            var Q6;
            Q6=makeQuery(id+"F3.imprint","IMPRINT",FACE,{"disambiguationData":[TD([[makeQuery(id+"F3.imprint","IMPRINT",EDGE,{"derivedFrom":sQuery(id+"F3.wireOp",EDGE,"E35.0")}),-1.0]])]});
            var Q7;
            {var subQ7=sQuery(id+"F3.wireOp",EDGE,"E3.2");Q7=makeQuery(id+"F3.imprint","IMPRINT",FACE,{"disambiguationData":[TD([[makeQuery(id+"F3.imprint","IMPRINT",EDGE,{"derivedFrom":subQ7}),-1.0]])]});}
            extrude(context, id + "F4", {"entities" : qUnion([Q0, Q1, Q2, Q3, Q4, Q5, Q6, Q7]), "depth" : 6 * mm});
        }
    });
